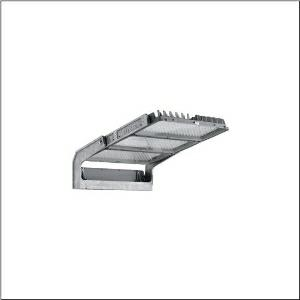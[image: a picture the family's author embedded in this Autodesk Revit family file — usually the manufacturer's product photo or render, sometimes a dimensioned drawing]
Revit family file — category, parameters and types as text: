
# Revit family: floodlight_fl_11_maxi_pro___rs08_5xa779224l01gb_ce58
name_source: partatom
category: Lighting Fixtures
units: mm (PartAtom-declared; Revit-internal decimal feet)

## family parameters
Cut with Voids When Loaded = No
Host = Face
Light Source = No
Part Type = Normal
Room Calculation Point = No
Round Connector Dimension = Use Diameter
Shared = No

## types (1)
- --- (1 x LED, 121700 lm, 1227.1 W, 5700K)
    Apparent Load = 1227 VA
    CIE Flux Codes = 70 87 98 100 100
    Color Rendering = 90
    Color Temperature = 5700K
    Default Elevation = 1800 mm
    Description = Floodlight FL 11  maxi  pro floodlight; light control with lens of PMMA; cover panel of toughened safety glass, transparent; light distribution: RS08, rotationally symmetric direct distribution, LEDcolour temperature: 5700K, rated luminous flux: 121.700lm, colour rendering: CRI > 90, light colour: 957; luminous efficacy: 99lm/W; brightness control: DMX+RDM; with terminal, 6-pole, max. 2.5mm², mains connection: 220..240V/380..400V AC, 50/60Hz, surge voltage resistance: line to ground: 10kV, service life up to 100,000h L90. Typical operating time: 1000h per year, ECG replaceable separately, LED unit replaceable without ESD environment, dustproof LED module, dimming range 10..100%; 1227W floodlight with 3x LED unit of diecast aluminium, coated grey; length: 1.003mm / width: 651mm / height: 338mm; mounting bracket, of diecast aluminium, uncoated, natural, protection rating (complete): IP66; insulation class (complete): insulation class I (protective earthing); certification: CE, ENEC, VDE; ball protection: ball impact resistant, only for outdoor installations in the designated locations, permissible operating ambient temperature: -45..+55°C, permissible storage temperature: -40..+85°Cpackaging unit: 1 piece

Light Distribution: RS08
    Height = 320 mm
    Lamp = 1 x LED
    Lamp Light Flux = 121700 lm
    Lamp Power = 1227.1 W
    Lamp count = 1
    Length = 1002 mm
    Luminous efficacy = 99 lm/W
    Manufacturer = Siteco
    ModVariant = No
    Model = 5XA779224L01GB
    Mounting Place = Ceiling
    Mounting Type = Surface mounted
    Number of Poles = 1
    OnlyDefault = Yes
    Power Factor = 1
    Product Name = Floodlight FL 11 maxi pro | RS08
    Product group = floodlight | ceiling mounted
    ProductGroupID = 301
    Protection Class = Protection class I
    Protection Degree = IP 66
    RLX_Detail_Level = 1
    RLX_Emergency_Light_Flux = 0 lm
    RLX_Emergency_Type = 0
    RLX_Emergency_Type_DB = No
    RlxData = <blob elided: 40169 chars, md5=7fe54228>
    Socket = socket
    Standby Power = 0 W
    System Light Flux = 121700 lm
    System Power = 1227 W
    Type Comments = factory setting: luminous flux: 100 % | dim-lin: 255 | 840 mA
    Type Image = l_1356210.jpg
    URL = http://relux.com
    VarID = @adj_014301
    Voltage = 0 V
    Weight = 0.00 kg
    Width = 655 mm

## geometry (parser evidence)
native form markers: Blend x4, Sweep x15
no freeform markers — native parametric forms only
